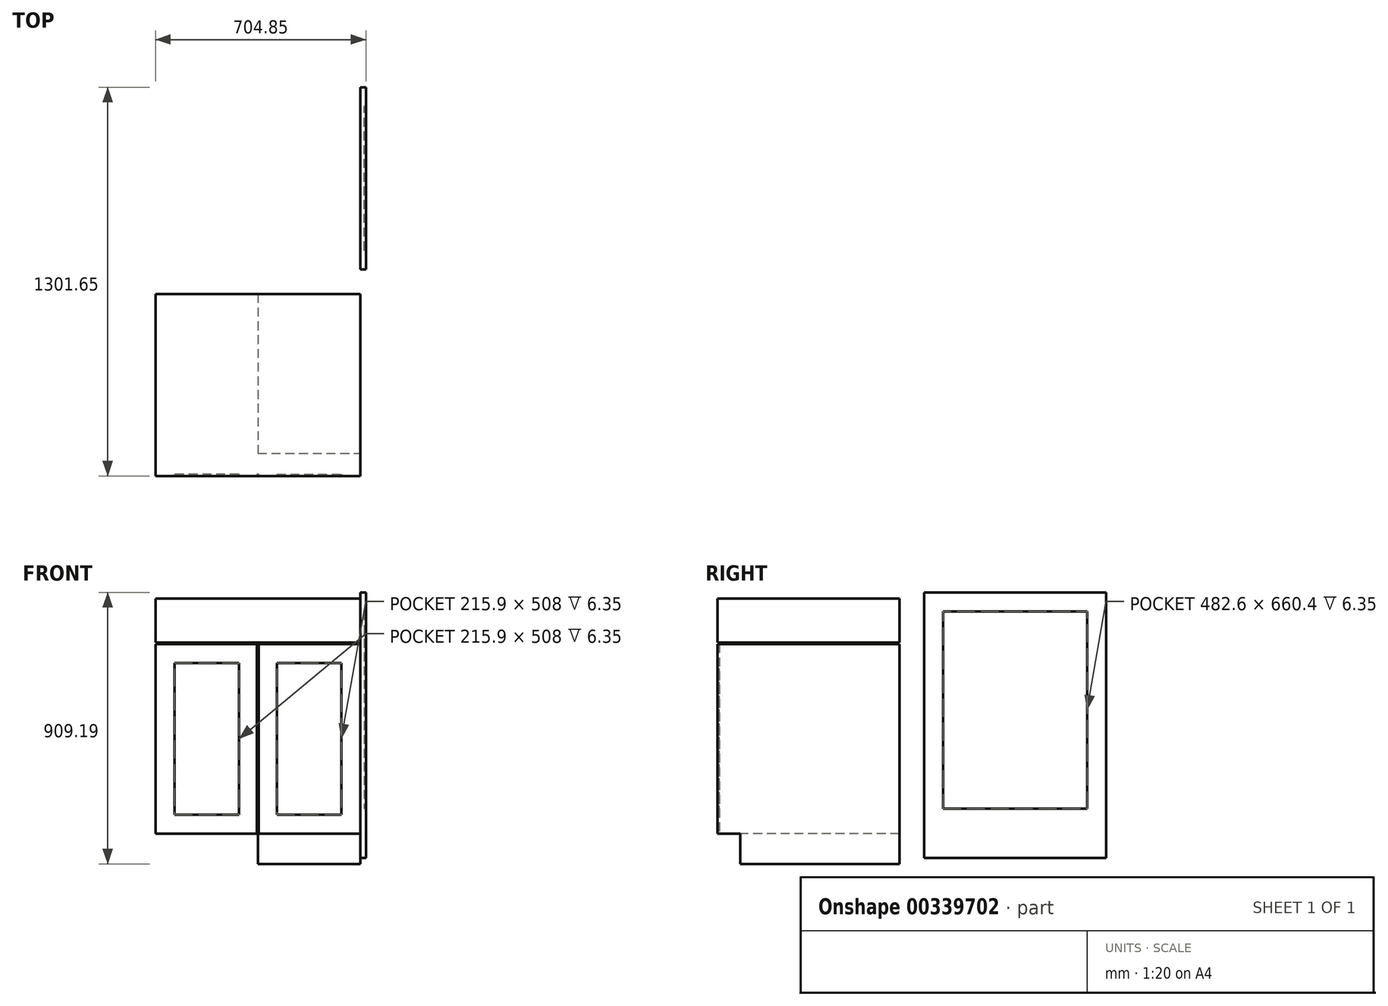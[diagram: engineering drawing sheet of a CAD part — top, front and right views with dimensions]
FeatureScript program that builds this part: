
annotation { "Feature Type Name" : "Feature", "Feature Type Description" : "" }
export const myFeature = defineFeature(function(context is Context, id is Id, definition is map)
    precondition{}
    {
        {
            var Q0;
            Q0=qCreatedBy(makeId("Front.planeOp"),FACE);
            var sketch = newSketch(context, id + "F0", { "sketchPlane" : qUnion([Q0])});
            skLineSegment(sketch, "E0.bottom", {"start": v(227.9, 0) * mm, "end": v(-115, 0) * mm});
            skLineSegment(sketch, "E0.top", {"start": v(227.9, 635) * mm, "end": v(-115, 635) * mm});
            skLineSegment(sketch, "E0.left", {"start": v(227.9, 0) * mm, "end": v(227.9, 635) * mm});
            skLineSegment(sketch, "E0.right", {"start": v(-115, 0) * mm, "end": v(-115, 635) * mm});
            skLineSegment(sketch, "E1.0", {"start": v(164.4, 571.5) * mm, "end": v(-51.5, 571.5) * mm});
            skLineSegment(sketch, "E1.1", {"start": v(164.4, 63.5) * mm, "end": v(164.4, 571.5) * mm});
            skLineSegment(sketch, "E1.2", {"start": v(164.4, 63.5) * mm, "end": v(-51.5, 63.5) * mm});
            skLineSegment(sketch, "E1.3", {"start": v(-51.5, 63.5) * mm, "end": v(-51.5, 571.5) * mm});
            skLineSegment(sketch, "E2.bottom", {"start": v(-115, 0) * mm, "end": v(227.9, 0) * mm});
            skLineSegment(sketch, "E2.top", {"start": v(-115, -101.6) * mm, "end": v(227.9, -101.6) * mm});
            skLineSegment(sketch, "E2.left", {"start": v(-115, 0) * mm, "end": v(-115, -101.6) * mm});
            skLineSegment(sketch, "E2.right", {"start": v(227.9, 0) * mm, "end": v(227.9, -101.6) * mm});
            skLineSegment(sketch, "E3.bottom", {"start": v(-115, 635) * mm, "end": v(227.9, 635) * mm});
            skLineSegment(sketch, "E3.top", {"start": v(-115, 787.4) * mm, "end": v(227.9, 787.4) * mm});
            skLineSegment(sketch, "E3.left", {"start": v(-115, 635) * mm, "end": v(-115, 787.4) * mm});
            skLineSegment(sketch, "E3.right", {"start": v(227.9, 635) * mm, "end": v(227.9, 787.4) * mm});
            skLineSegment(sketch, "E4.top", {"start": v(-115, 640.08) * mm, "end": v(227.9, 640.08) * mm});
            skLineSegment(sketch, "E4.left", {"start": v(-115, 635) * mm, "end": v(-115, 640.08) * mm});
            skLineSegment(sketch, "E4.right", {"start": v(227.9, 635) * mm, "end": v(227.9, 640.08) * mm});
            skLineSegment(sketch, "E5.MirrorCS", {"start": v(570.8, 635) * mm, "end": v(570.8, 640.08) * mm});
            skLineSegment(sketch, "E6.MirrorCS", {"start": v(227.9, 635) * mm, "end": v(570.8, 635) * mm});
            skLineSegment(sketch, "E7.MirrorCS", {"start": v(570.8, 635) * mm, "end": v(227.9, 635) * mm});
            skLineSegment(sketch, "E8.MirrorCS", {"start": v(227.9, 0) * mm, "end": v(570.8, 0) * mm});
            skLineSegment(sketch, "E9.MirrorCS", {"start": v(570.8, 0) * mm, "end": v(570.8, -101.6) * mm});
            skLineSegment(sketch, "E10.MirrorCS", {"start": v(570.8, -101.6) * mm, "end": v(227.9, -101.6) * mm});
            skLineSegment(sketch, "E11.MirrorCS", {"start": v(570.8, 0) * mm, "end": v(227.9, 0) * mm});
            skLineSegment(sketch, "E12.MirrorCS", {"start": v(507.3, 63.5) * mm, "end": v(507.3, 571.5) * mm});
            skLineSegment(sketch, "E13.MirrorCS", {"start": v(291.4, 63.5) * mm, "end": v(507.3, 63.5) * mm});
            skLineSegment(sketch, "E14.MirrorCS", {"start": v(291.4, 63.5) * mm, "end": v(291.4, 571.5) * mm});
            skLineSegment(sketch, "E15.MirrorCS", {"start": v(291.4, 571.5) * mm, "end": v(507.3, 571.5) * mm});
            skLineSegment(sketch, "E16.MirrorCS", {"start": v(570.8, 0) * mm, "end": v(570.8, 635) * mm});
            skLineSegment(sketch, "E17.MirrorCS", {"start": v(570.8, 635) * mm, "end": v(570.8, 787.4) * mm});
            skLineSegment(sketch, "E18.MirrorCS", {"start": v(570.8, 640.08) * mm, "end": v(227.9, 640.08) * mm});
            skLineSegment(sketch, "E19.MirrorCS", {"start": v(570.8, 787.4) * mm, "end": v(227.9, 787.4) * mm});
            skLineSegment(sketch, "E20", {"start": v(224.73, 635) * mm, "end": v(224.73, 0) * mm});
            skLineSegment(sketch, "E21", {"start": v(231.08, 635) * mm, "end": v(231.08, 0) * mm});
            skSolve(sketch);
        }
        {
            var Q0;
            Q0=makeQuery(id+"F0.imprint","IMPRINT",FACE,{"disambiguationData":[TD([[makeQuery(id+"F0.imprint","IMPRINT",EDGE,{"derivedFrom":sQuery(id+"F0.wireOp",EDGE,"E1.0")}),1.0]])]});
            var Q1;
            Q1=makeQuery(id+"F0.imprint","IMPRINT",FACE,{"disambiguationData":[TD([[makeQuery(id+"F0.imprint","IMPRINT",EDGE,{"derivedFrom":sQuery(id+"F0.wireOp",EDGE,"E2.bottom")}),-1.0]])]});
            var Q2;
            Q2=makeQuery(id+"F0.imprint","IMPRINT",FACE,{"disambiguationData":[TD([[makeQuery(id+"F0.imprint","IMPRINT",EDGE,{"derivedFrom":sQuery(id+"F0.wireOp",EDGE,"E0.left")}),1.0]])]});
            var Q3;
            {var subQ0=sQuery(id+"F0.wireOp",EDGE,"E3.top");Q3=makeQuery(id+"F0.imprint","IMPRINT",FACE,{"disambiguationData":[TD([[makeQuery(id+"F0.imprint","IMPRINT",EDGE,{"derivedFrom":subQ0}),-1.0]])]});}
            var Q4;
            {var subQ0=sQuery(id+"F0.wireOp",EDGE,"E3.bottom");Q4=makeQuery(id+"F0.imprint","IMPRINT",FACE,{"disambiguationData":[TD([[makeQuery(id+"F0.imprint","IMPRINT",EDGE,{"derivedFrom":subQ0}),1.0]])]});}
            var Q5;
            Q5=makeQuery(id+"F0.imprint","IMPRINT",FACE,{"disambiguationData":[TD([[makeQuery(id+"F0.imprint","IMPRINT",EDGE,{"derivedFrom":sQuery(id+"F0.wireOp",EDGE,"E12.MirrorCS")}),1.0]])]});
            var Q6;
            {var subQ2=sQuery(id+"F0.wireOp",EDGE,"E18.MirrorCS");Q6=makeQuery(id+"F0.imprint","IMPRINT",FACE,{"disambiguationData":[TD([[makeQuery(id+"F0.imprint","IMPRINT",EDGE,{"derivedFrom":subQ2}),-1.0]])]});}
            var Q7;
            Q7=makeQuery(id+"F0.imprint","IMPRINT",FACE,{"disambiguationData":[TD([[makeQuery(id+"F0.imprint","IMPRINT",EDGE,{"derivedFrom":sQuery(id+"F0.wireOp",EDGE,"E2.right")}),1.0]])]});
            var Q8;
            Q8=makeQuery(id+"F0.imprint","IMPRINT",FACE,{"disambiguationData":[TD([[makeQuery(id+"F0.imprint","IMPRINT",EDGE,{"derivedFrom":sQuery(id+"F0.wireOp",EDGE,"E0.left")}),-1.0]])]});
            var Q9;
            {var subQ0=sQuery(id+"F0.wireOp",EDGE,"E7.MirrorCS");Q9=makeQuery(id+"F0.imprint","IMPRINT",FACE,{"disambiguationData":[TD([[makeQuery(id+"F0.imprint","IMPRINT",EDGE,{"derivedFrom":subQ0}),-1.0]])]});}
            var Q10;
            {var subQ0=sQuery(id+"F0.wireOp",EDGE,"E0.right");Q10=makeQuery(id+"F0.imprint","IMPRINT",FACE,{"disambiguationData":[TD([[makeQuery(id+"F0.imprint","IMPRINT",EDGE,{"derivedFrom":subQ0}),-1.0]])]});}
            var Q11;
            Q11=makeQuery(id+"F0.imprint","IMPRINT",FACE,{"disambiguationData":[TD([[makeQuery(id+"F0.imprint","IMPRINT",EDGE,{"derivedFrom":sQuery(id+"F0.wireOp",EDGE,"E12.MirrorCS")}),-1.0]])]});
            extrude(context, id + "F1", {"entities" : qUnion([Q0, Q1, Q2, Q3, Q4, Q5, Q6, Q7, Q8, Q9, Q10, Q11]), "oppositeDirection" : true, "depth" : 609.6 * mm});
        }
        {
            var Q0;
            Q0=makeQuery(id+"F0.imprint","IMPRINT",FACE,{"disambiguationData":[TD([[makeQuery(id+"F0.imprint","IMPRINT",EDGE,{"derivedFrom":sQuery(id+"F0.wireOp",EDGE,"E1.0")}),1.0]])]});
            var Q1;
            Q1=makeQuery(id+"F0.imprint","IMPRINT",FACE,{"disambiguationData":[TD([[makeQuery(id+"F0.imprint","IMPRINT",EDGE,{"derivedFrom":sQuery(id+"F0.wireOp",EDGE,"E3.bottom")}),1.0]])]});
            var Q2;
            Q2=makeQuery(id+"F0.imprint","IMPRINT",FACE,{"disambiguationData":[TD([[makeQuery(id+"F0.imprint","IMPRINT",EDGE,{"derivedFrom":sQuery(id+"F0.wireOp",EDGE,"E12.MirrorCS")}),1.0]])]});
            var Q3;
            {var subQ0=sQuery(id+"F0.wireOp",EDGE,"E7.MirrorCS");Q3=makeQuery(id+"F0.imprint","IMPRINT",FACE,{"disambiguationData":[TD([[makeQuery(id+"F0.imprint","IMPRINT",EDGE,{"derivedFrom":subQ0}),-1.0]])]});}
            var Q4;
            {var subQ0=sQuery(id+"F0.wireOp",EDGE,"E0.left");Q4=makeQuery(id+"F0.imprint","IMPRINT",FACE,{"disambiguationData":[TD([[makeQuery(id+"F0.imprint","IMPRINT",EDGE,{"derivedFrom":subQ0}),1.0]])]});}
            var Q5;
            {var subQ0=sQuery(id+"F0.wireOp",EDGE,"E0.left");Q5=makeQuery(id+"F0.imprint","IMPRINT",FACE,{"disambiguationData":[TD([[makeQuery(id+"F0.imprint","IMPRINT",EDGE,{"derivedFrom":subQ0}),-1.0]])]});}
            extrude(context, id + "F2", {"entities" : qUnion([Q0, Q1, Q2, Q3, Q4, Q5]), "operationType" : NewBodyOperationType.REMOVE, "oppositeDirection" : true, "depth" : 6.35 * mm});
        }
        {
            var Q0;
            Q0=makeQuery(id+"F0.imprint","IMPRINT",FACE,{"disambiguationData":[TD([[makeQuery(id+"F0.imprint","IMPRINT",EDGE,{"derivedFrom":sQuery(id+"F0.wireOp",EDGE,"E2.bottom")}),-1.0]])]});
            var Q1;
            Q1=makeQuery(id+"F0.imprint","IMPRINT",FACE,{"disambiguationData":[TD([[makeQuery(id+"F0.imprint","IMPRINT",EDGE,{"derivedFrom":sQuery(id+"F0.wireOp",EDGE,"E2.right")}),1.0]])]});
            extrude(context, id + "F3", {"entities" : qUnion([Q0, Q1]), "operationType" : NewBodyOperationType.REMOVE, "oppositeDirection" : true, "depth" : 76.2 * mm});
        }
        {
            var Q0;
            Q0=makeQuery(id+"F1.opExtrude","SWEPT_FACE",FACE,{"disambiguationData":[OSD([sQuery(id+"F0.wireOp",EDGE,"E9.MirrorCS"),sQuery(id+"F0.wireOp",EDGE,"E16.MirrorCS"),sQuery(id+"F0.wireOp",EDGE,"E17.MirrorCS")])]});
            var sketch = newSketch(context, id + "F4", { "sketchPlane" : qUnion([Q0])});
            skLineSegment(sketch, "E22.bottom", {"start": v(692.05, 807.6) * mm, "end": v(1301.65, 807.6) * mm});
            skLineSegment(sketch, "E22.top", {"start": v(692.05, -81.4) * mm, "end": v(1301.65, -81.4) * mm});
            skLineSegment(sketch, "E22.left", {"start": v(692.05, 807.6) * mm, "end": v(692.05, -81.4) * mm});
            skLineSegment(sketch, "E22.right", {"start": v(1301.65, 807.6) * mm, "end": v(1301.65, -81.4) * mm});
            skLineSegment(sketch, "E23.0", {"start": v(1238.15, 744.1) * mm, "end": v(1238.15, 83.7) * mm});
            skLineSegment(sketch, "E23.1", {"start": v(755.55, 744.1) * mm, "end": v(1238.15, 744.1) * mm});
            skLineSegment(sketch, "E23.2", {"start": v(755.55, 744.1) * mm, "end": v(755.55, 83.7) * mm});
            skLineSegment(sketch, "E23.3", {"start": v(755.55, 83.7) * mm, "end": v(1238.15, 83.7) * mm});
            skSolve(sketch);
        }
        {
            var Q0;
            Q0=makeQuery(id+"F4.imprint","IMPRINT",FACE,{"disambiguationData":[TD([[makeQuery(id+"F4.imprint","IMPRINT",EDGE,{"derivedFrom":sQuery(id+"F4.wireOp",EDGE,"E22.bottom")}),-1.0]])]});
            extrude(context, id + "F5", {"entities" : qUnion([Q0]), "depth" : 19.05 * mm, "offsetDistance" : 25.4 * mm});
        }
        {
            var Q0;
            Q0=makeQuery(id+"F4.imprint","IMPRINT",FACE,{"disambiguationData":[TD([[makeQuery(id+"F4.imprint","IMPRINT",EDGE,{"derivedFrom":sQuery(id+"F4.wireOp",EDGE,"E23.0")}),-1.0]])]});
            extrude(context, id + "F6", {"entities" : qUnion([Q0]), "operationType" : NewBodyOperationType.ADD, "depth" : 12.7 * mm, "offsetDistance" : 25.4 * mm});
        }
    });
